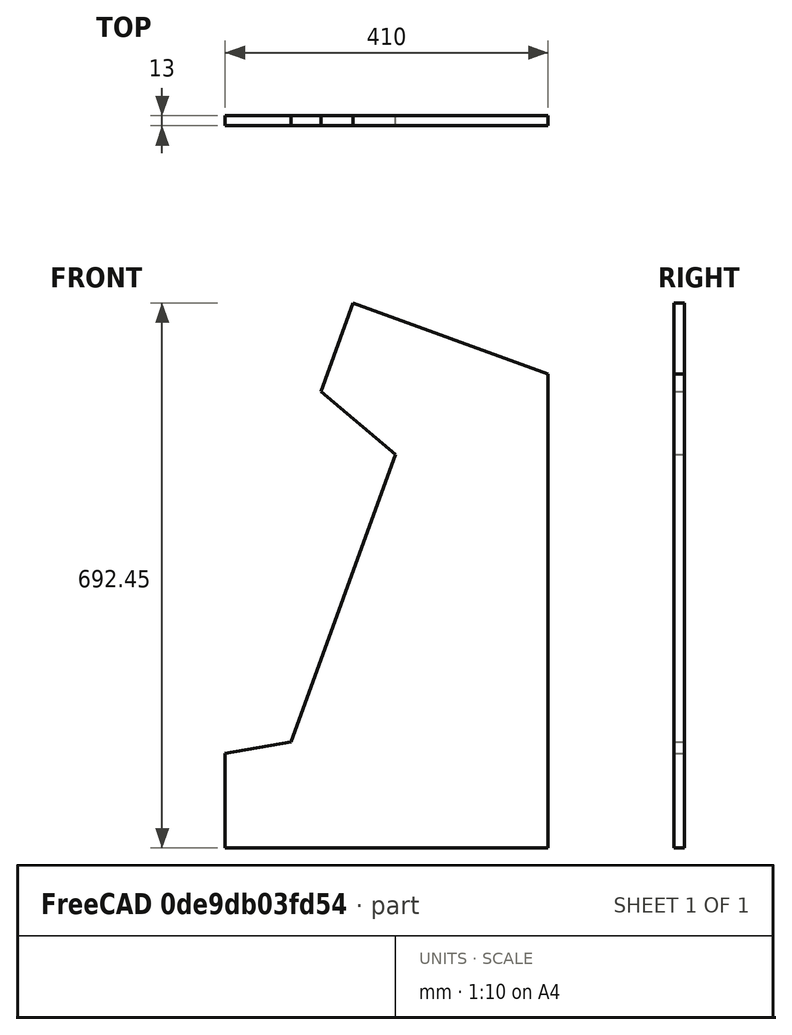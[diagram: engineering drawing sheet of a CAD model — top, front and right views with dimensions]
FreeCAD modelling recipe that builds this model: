
FCSTD DOCUMENT  (FreeCAD 0.18R16131 (Git))
Label: 9000_Profile_Sidewall
License: All rights reserved
LicenseURL: http://en.wikipedia.org/wiki/All_rights_reserved
objects: Sketcher::SketchObject×1, PartDesign::Pad×1, PartDesign::Body×1, Spreadsheet::Sheet×1
note: 4 computed .brp shape members not serialized (recipe doc carries the construction recipe); baked Part::Feature solids carry a one-line shape summary decoded from their .brp

FEATURE [Sketcher::SketchObject] Sketch  label="SideWall"
  MapMode = 5
  Placement = pos=(0,0,0) rot=(1,0,0;1.5708rad)
  Support = -> [XZ_Plane]
  expr: Constraints[5] = XLS.TH
  expr: Constraints[1] = XLS.TW
  sketch-geometry (13):
    g0: LineSegment StartX=0 StartY=0 StartZ=0 EndX=280 EndY=0 EndZ=0
    g1: LineSegment [constr] StartX=280 StartY=445.46 StartZ=0 EndX=86.4277 EndY=500 EndZ=0
    g2: LineSegment StartX=86.4277 StartY=500 StartZ=0 EndX=-46.5237 EndY=134.719 EndZ=0
    g3: LineSegment [constr] StartX=280 StartY=445.46 StartZ=0 EndX=280 EndY=500 EndZ=0
    g4: LineSegment [constr] StartX=280 StartY=500 StartZ=0 EndX=86.4277 EndY=500 EndZ=0
    g5: LineSegment StartX=280 StartY=0 StartZ=0 EndX=280 EndY=445.46 EndZ=0
    g6: LineSegment StartX=0 StartY=0 StartZ=0 EndX=-130 EndY=0 EndZ=0
    g7: LineSegment StartX=-130 StartY=0 StartZ=0 EndX=-130 EndY=120 EndZ=0
    g8: LineSegment StartX=-130 StartY=120 StartZ=0 EndX=-46.5237 EndY=134.719 EndZ=0
    g9: LineSegment StartX=280 StartY=445.46 StartZ=0 EndX=280 EndY=602.368 EndZ=0
    g10: LineSegment StartX=280 StartY=602.368 StartZ=0 EndX=32.5036 EndY=692.449 EndZ=0
    g11: LineSegment StartX=32.5036 StartY=692.449 StartZ=0 EndX=-8.53882 EndY=579.686 EndZ=0
    g12: LineSegment StartX=-8.53882 StartY=579.686 StartZ=0 EndX=86.4277 EndY=500 EndZ=0
  constraints (35):
    c: Coincident(g1,g2)
    c: DistanceX(g0,g0) = 280
    c: Angle(g0,g2) = 1.22173
    c: Coincident(g4,g3)
    c: Coincident(g4,g1)
    c: DistanceY(g0,g3) = 500
    c: PointOnObject(g0,g-2)
    c: Horizontal(g0)
    c: Coincident(g5,g0)
    c: Coincident(g5,g1)
    c: Vertical(g5)
    c: Coincident(g3,g1)
    c: Vertical(g3)
    c: PointOnObject(g0,g-1)
    c: Perpendicular(g3,g4)
    c: Coincident(g6,g0)
    c: PointOnObject(g6,g-1)
    c: Coincident(g7,g6)
    c: Vertical(g7)
    c: Coincident(g8,g7)
    c: Coincident(g8,g2)
    c: Coincident(g9,g5)
    c: Vertical(g9)
    c: Coincident(g10,g9)
    c: Coincident(g11,g10)
    c: Coincident(g12,g11)
    c: Coincident(g12,g2)
    c: Perpendicular(g11,g10)
    c: Distance(g11) = 120
    c: Distance(g12) = 123.97
    c: Angle(g12,g2) = 1.91986
    c: Angle(g10,g9) = 1.91986
    c: Angle(g2,g8) = 2.0944
    c: DistanceY(g7,g7) = 120
    c: DistanceX(g6,g6) = 130
FEATURE [PartDesign::Pad] Pad
  Length = 13
  Length2 = 100
  Placement = pos=(0,0,0) rot=(1,0,0;1.5708rad)
  Profile = -> Sketch
  Reversed = true
  Type = 0
FEATURE [PartDesign::Body] Body
  Group = -> [Sketch,Pad]
  Origin = -> Origin
  Tip = -> Pad
FEATURE [Spreadsheet::Sheet] Spreadsheet  label="XLS"
  cells = B3=SideWall.; B4=Width; C4=TW; D4(TW)=280; E4=mm; B5=Total Height; C5=TH; D5(TH)=500; E5=mm; B6=Thickness; C6=T; D6(T)=13; E6=mm; B7=Front Height; C7=FH; D7(FH)=115; E7=mm
